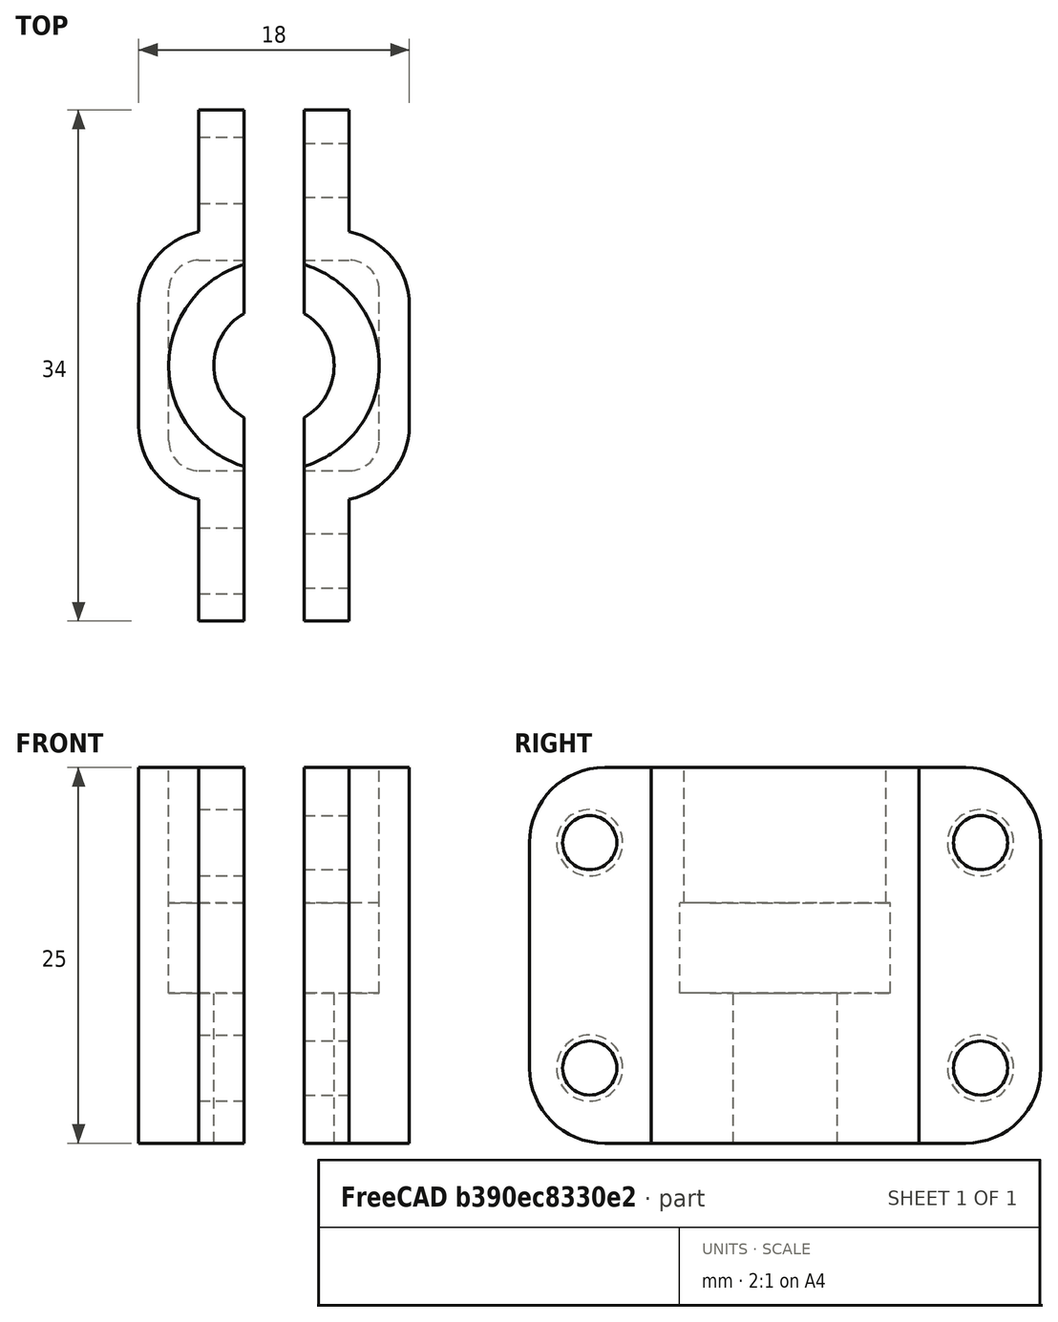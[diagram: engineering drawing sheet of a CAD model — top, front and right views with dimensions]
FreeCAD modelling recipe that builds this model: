
FCSTD DOCUMENT  (FreeCAD 0.19R)
Label: heater_gun_protector
License: All rights reserved
LicenseURL: http://en.wikipedia.org/wiki/All_rights_reserved
objects: Part::MultiFuse×6, Part::Cylinder×4, Part::Box×4, Part::Mirroring×4, Part::Fillet×3, Part::Cut×1
note: 22 computed .brp shape members not serialized (recipe doc carries the construction recipe); baked Part::Feature solids carry a one-line shape summary decoded from their .brp

FEATURE [Part::Cylinder] Cylinder  label="wire hole"
  Angle = 360
  AttacherType = Attacher::AttachEngine3D
  Height = 10
  Radius = 4
FEATURE [Part::Cylinder] Cylinder001  label="body hole"
  Angle = 360
  AttacherType = Attacher::AttachEngine3D
  Height = 15
  Placement = pos=(0,0,10) rot=(0,0,1;0rad)
  Radius = 7
  expr: .Placement.Base.z = <<wire hole>>.Height
FEATURE [Part::Box] Box  label="body cube"
  AttacherType = Attacher::AttachEngine3D
  Height = 25
  Length = 18
  Placement = pos=(-9,-9,0) rot=(0,0,1;0rad)
  Width = 18
  expr: .Placement.Base.y = -Width / 2
  expr: .Placement.Base.x = -Length / 2
  expr: Height = <<wire hole>>.Height + <<body hole>>.Height
FEATURE [Part::Fillet] Fillet  label="body fillet"
  Base = -> Box
  Edges = 4 edges r=5: [Edge1,Edge3,Edge5,Edge7]
FEATURE [Part::Box] Box001  label="split cube"
  AttacherType = Attacher::AttachEngine3D
  Height = 25
  Length = 4
  Placement = pos=(-2,-17,0) rot=(0,0,1;0rad)
  Width = 34
  expr: Width = <<body cube>>.Width + 16mm
  expr: Height = <<body cube>>.Height
  expr: .Placement.Base.x = -Length / 2
  expr: .Placement.Base.y = -Width / 2
FEATURE [Part::Box] Box002  label="ear cube"
  AttacherType = Attacher::AttachEngine3D
  Height = 25
  Length = 10
  Placement = pos=(-5,-17,0) rot=(0,0,1;0rad)
  Width = 34
  expr: Length = <<split cube>>.Length + 6mm
  expr: .Placement.Base.y = -Width / 2
  expr: .Placement.Base.x = -Length / 2
  expr: Height = <<body cube>>.Height
  expr: Width = <<split cube>>.Width
FEATURE [Part::Fillet] Fillet001  label="ear cube fillet"
  Base = -> Box002
  Edges = 4 edges r=5: [Edge9,Edge10,Edge11,Edge12]
FEATURE [Part::Cylinder] Cylinder002  label="bolt hole"
  Angle = 360
  AttacherType = Attacher::AttachEngine3D
  Height = 5
  Placement = pos=(0,0,5) rot=(0,1,0;1.5708rad)
  Radius = 1.8
  expr: Height = <<ear cube>>.Length / 2
FEATURE [Part::Mirroring] Part__Mirroring  label="bolt hole (Mirror #1)"
  Base = (0,0,12.5)
  Normal = (0,0,1)
  Source = -> Cylinder002
  expr: .Base.z = <<body cube>>.Height / 2
FEATURE [Part::MultiFuse] Fusion  label="bolt hole fusion"
  Placement = pos=(0,13,0) rot=(0,0,1;0rad)
  Shapes = -> [Part__Mirroring,Cylinder002]
  expr: .Placement.Base.y = (<<body cube>>.Width + <<ear cube>>.Width) / 4
FEATURE [Part::Mirroring] Part__Mirroring001  label="bolt hole fusion (Mirror #2)"
  Base = (0,0,0)
  Normal = (0,1,0)
  Source = -> Fusion
FEATURE [Part::MultiFuse] Fusion001  label="4 bolt hole fusion"
  Shapes = -> [Part__Mirroring001,Fusion]
FEATURE [Part::MultiFuse] Fusion002  label="body fusion"
  Shapes = -> [Fillet,Fillet001]
FEATURE [Part::Box] Box003  label="center hole cube"
  AttacherType = Attacher::AttachEngine3D
  Height = 6
  Length = 14
  Placement = pos=(-7,-7,10) rot=(0,0,1;0rad)
  Width = 14
  expr: .Placement.Base.z = <<wire hole>>.Height
  expr: .Placement.Base.y = -Width / 2
  expr: .Placement.Base.x = -Length / 2
FEATURE [Part::Fillet] Fillet002  label="center hole cube fillet"
  Base = -> Box003
  Edges = 4 edges r=2: [Edge1,Edge3,Edge5,Edge7]
FEATURE [Part::Cylinder] Cylinder003  label="insert hole"
  Angle = 360
  AttacherType = Attacher::AttachEngine3D
  Height = 5
  Placement = pos=(-5,0,5) rot=(0,1,0;1.5708rad)
  Radius = 2.2
  expr: .Placement.Base.x = -Height
  expr: Height = <<ear cube>>.Length / 2
FEATURE [Part::Mirroring] Part__Mirroring002  label="insert hole (Mirror #1)"
  Base = (0,0,12.5)
  Normal = (0,0,1)
  Source = -> Cylinder003
  expr: .Base.z = <<body cube>>.Height / 2
FEATURE [Part::MultiFuse] Fusion005  label="insert hole fusion"
  Placement = pos=(0,13,0) rot=(0,0,1;0rad)
  Shapes = -> [Cylinder003,Part__Mirroring002]
  expr: .Placement.Base.y = (<<body cube>>.Width + <<ear cube>>.Width) / 4
FEATURE [Part::Mirroring] Part__Mirroring003  label="insert hole fusion (Mirror #2)"
  Base = (0,0,0)
  Normal = (0,1,0)
  Source = -> Fusion005
FEATURE [Part::MultiFuse] Fusion006  label="4 insert hole fusion"
  Shapes = -> [Fusion005,Part__Mirroring003]
FEATURE [Part::MultiFuse] Fusion003  label="hole fusion"
  Shapes = -> [Cylinder,Cylinder001,Box001,Fillet002,Fusion001,Fusion006]
FEATURE [Part::Cut] Cut  label="body cut"
  Base = -> Fusion002
  Tool = -> Fusion003
